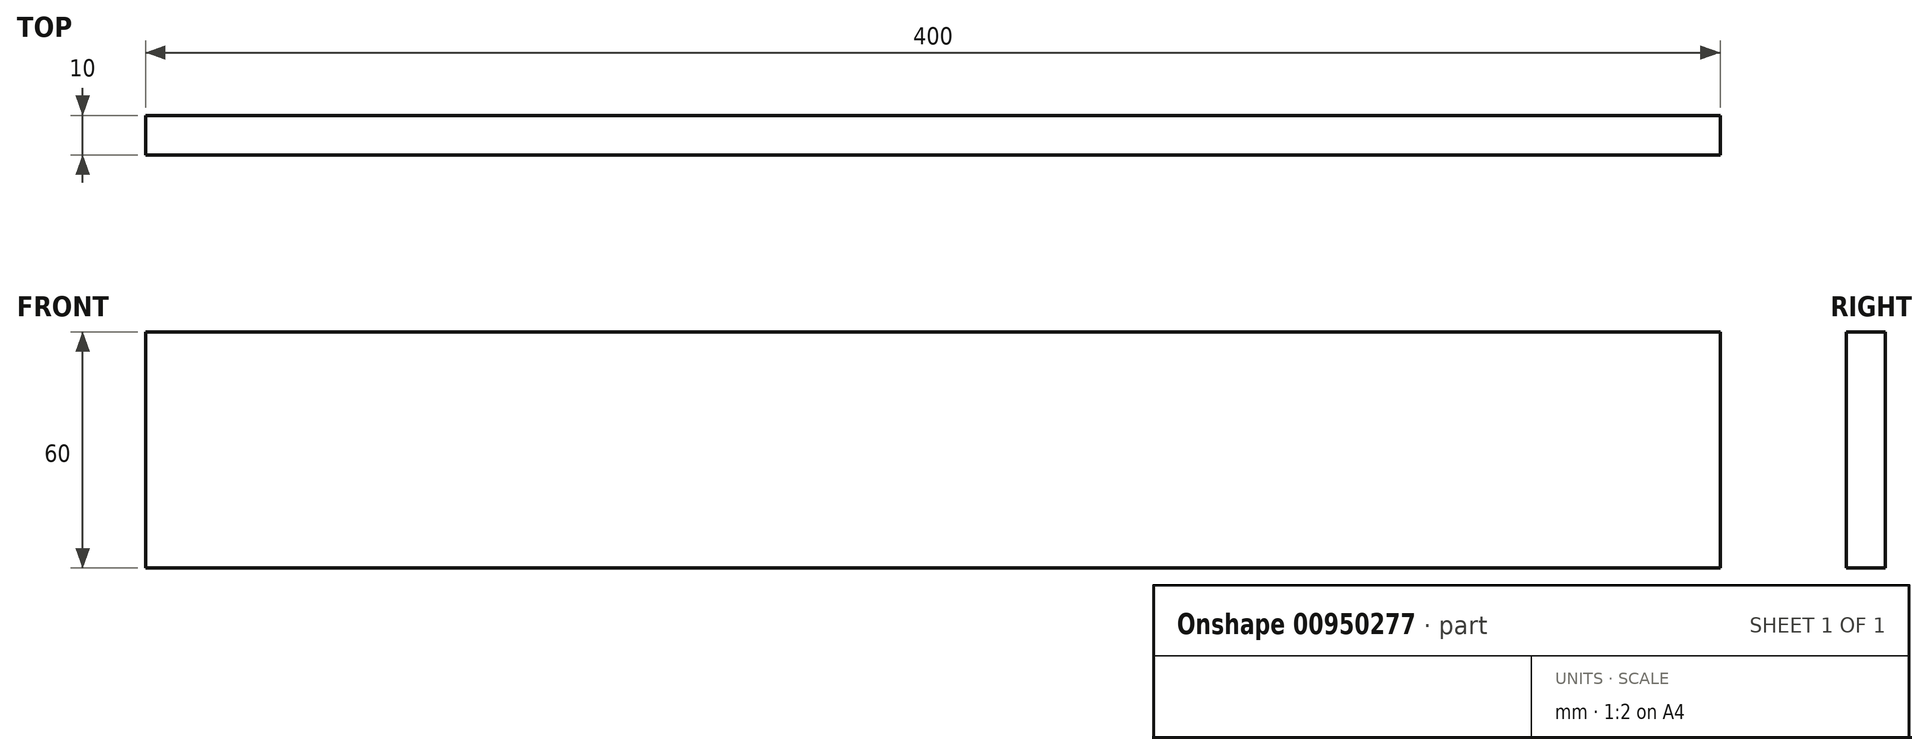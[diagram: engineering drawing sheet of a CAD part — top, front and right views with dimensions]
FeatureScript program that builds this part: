
annotation { "Feature Type Name" : "Feature", "Feature Type Description" : "" }
export const myFeature = defineFeature(function(context is Context, id is Id, definition is map)
    precondition{}
    {
        {
            var Q0;
            Q0=qCreatedBy(makeId("Front.planeOp"),FACE);
            var sketch = newSketch(context, id + "F0", { "sketchPlane" : qUnion([Q0])});
            skLineSegment(sketch, "E0.bottom", {"start": v(200, -30) * mm, "end": v(-200, -30) * mm});
            skLineSegment(sketch, "E0.top", {"start": v(200, 30) * mm, "end": v(-200, 30) * mm});
            skLineSegment(sketch, "E0.left", {"start": v(200, -30) * mm, "end": v(200, 30) * mm});
            skLineSegment(sketch, "E0.right", {"start": v(-200, -30) * mm, "end": v(-200, 30) * mm});
            skPoint(sketch, "E0.middle", {"position": v(0, 0) * mm});
            skSolve(sketch);
        }
        {
            var Q0;
            Q0=makeQuery(id+"F0.imprint","IMPRINT",FACE,{"disambiguationData":[TD([[makeQuery(id+"F0.imprint","IMPRINT",EDGE,{"derivedFrom":sQuery(id+"F0.wireOp",EDGE,"E0.bottom")}),-1.0]])]});
            extrude(context, id + "F1", {"entities" : qUnion([Q0]), "endBound" : BoundingType.SYMMETRIC, "depth" : 10 * mm, "offsetDistance" : 25 * mm});
        }
    });
